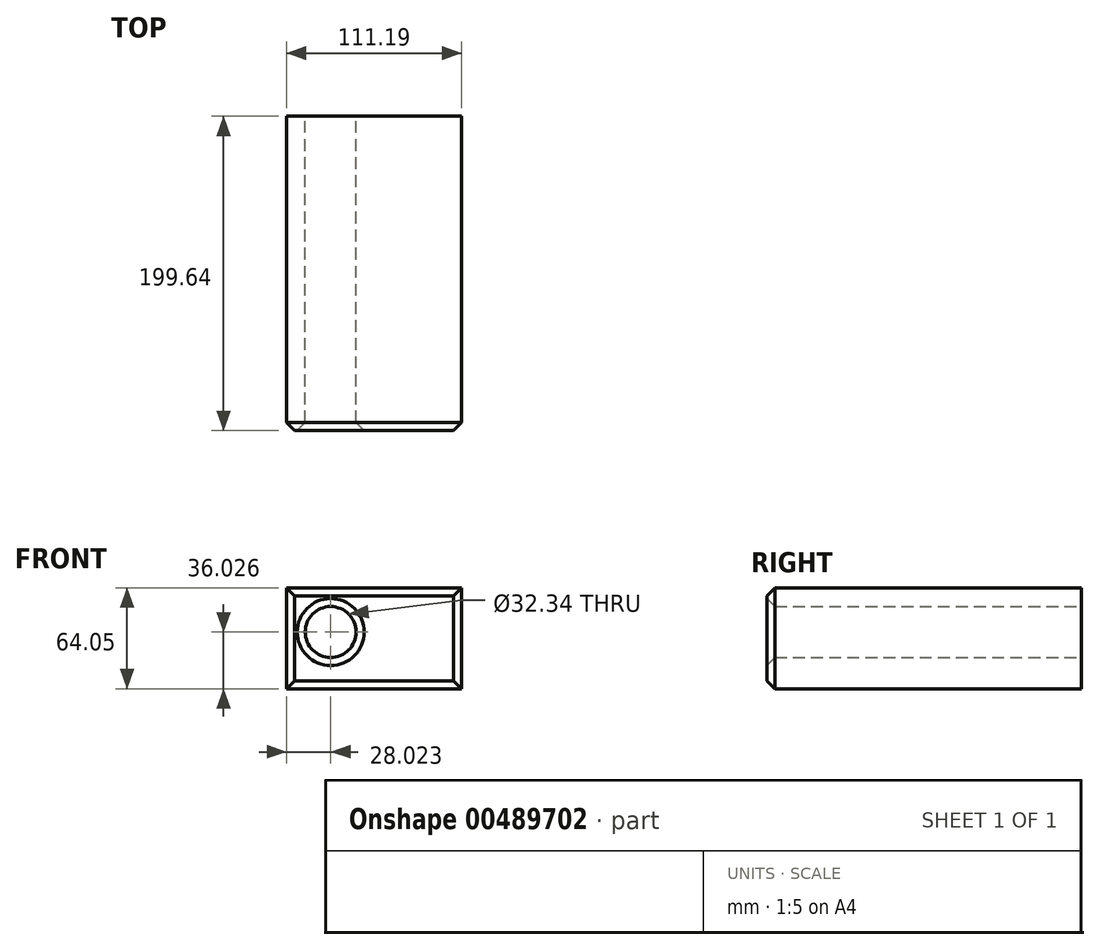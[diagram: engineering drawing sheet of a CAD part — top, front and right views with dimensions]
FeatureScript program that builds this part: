
annotation { "Feature Type Name" : "Feature", "Feature Type Description" : "" }
export const myFeature = defineFeature(function(context is Context, id is Id, definition is map)
    precondition{}
    {
        {
            var Q0;
            Q0=qCreatedBy(makeId("Front.planeOp"),FACE);
            var sketch = newSketch(context, id + "F0", { "sketchPlane" : qUnion([Q0])});
            skLineSegment(sketch, "E0.bottom", {"start": v(-129.12, -7.78) * mm, "end": v(-17.93, -7.78) * mm});
            skLineSegment(sketch, "E0.top", {"start": v(-129.12, -71.83) * mm, "end": v(-17.93, -71.83) * mm});
            skLineSegment(sketch, "E0.left", {"start": v(-129.12, -7.78) * mm, "end": v(-129.12, -71.83) * mm});
            skLineSegment(sketch, "E0.right", {"start": v(-17.93, -7.78) * mm, "end": v(-17.93, -71.83) * mm});
            skCircle(sketch, "E1", {"center": v(-101.1, -35.8) * mm, "radius": 16.17 * mm});
            skSolve(sketch);
        }
        {
            var Q0;
            Q0 = qSketchRegion(id + "F0", true);
            extrude(context, id + "F1", {"entities" : qUnion([Q0]), "depth" : 199.64 * mm});
        }
        {
            var Q0;
            Q0=makeQuery(id+"F1.opExtrude","CAP_FACE",FACE,{"disambiguationData":[OSD([sQuery(id+"F0.wireOp",EDGE,"E0.bottom"),sQuery(id+"F0.wireOp",EDGE,"E0.top"),sQuery(id+"F0.wireOp",EDGE,"E0.left"),sQuery(id+"F0.wireOp",EDGE,"E0.right"),sQuery(id+"F0.wireOp",EDGE,"E1")])],"isStart":false});
            chamfer(context, id + "F2", {"entities" : qUnion([Q0]), "width" : 5.08 * mm, "tangentPropagation" : true});
        }
        {
            var Q0;
            Q0=makeQuery(id+"F1.opExtrude","CAP_FACE",FACE,{"disambiguationData":[OSD([sQuery(id+"F0.wireOp",EDGE,"E0.bottom"),sQuery(id+"F0.wireOp",EDGE,"E0.top"),sQuery(id+"F0.wireOp",EDGE,"E0.left"),sQuery(id+"F0.wireOp",EDGE,"E0.right"),sQuery(id+"F0.wireOp",EDGE,"E1")])],"isStart":false});
            var sketch = newSketch(context, id + "F3", { "sketchPlane" : qUnion([Q0])});
            skLineSegment(sketch, "E2.bottom", {"start": v(-63.24, -25.15) * mm, "end": v(-40.18, -25.15) * mm});
            skLineSegment(sketch, "E2.top", {"start": v(-63.24, -55.7) * mm, "end": v(-40.18, -55.7) * mm});
            skLineSegment(sketch, "E2.left", {"start": v(-63.24, -25.15) * mm, "end": v(-63.24, -55.7) * mm});
            skLineSegment(sketch, "E2.right", {"start": v(-40.18, -25.15) * mm, "end": v(-40.18, -55.7) * mm});
            skArc(sketch, "E3", {"start": v(-63.24, -41) * mm, "mid": v(-60.74, -57.72) * mm, "end": v(-43.95, -55.7) * mm});
            skSolve(sketch);
        }
        {
            var Q0;
            {var subQ0=sQuery(id+"F3.wireOp",EDGE,"E2.left");var subQ1=sQuery(id+"F3.wireOp",EDGE,"E2.top");var subQ2=makeQuery(id+"F3.imprint","INTERSECT",VERTEX,{"derivedFrom":[subQ1,subQ0]});Q0=makeQuery(id+"F3.imprint","IMPRINT",FACE,{"disambiguationData":[TD([[makeQuery(id+"F3.imprint","IMPRINT",EDGE,{"disambiguationData":[TD([[subQ2,-1.0]])],"derivedFrom":subQ1}),1.0]])]});}
            var Q1;
            {var subQ0=sQuery(id+"F3.wireOp",EDGE,"E3");var subQ1=sQuery(id+"F3.wireOp",EDGE,"E2.top");var subQ2=makeQuery(id+"F3.imprint","INTERSECT",VERTEX,{"disambiguationData":[OD(0.0)],"derivedFrom":[subQ1,subQ0]});Q1=makeQuery(id+"F3.imprint","IMPRINT",FACE,{"disambiguationData":[TD([[makeQuery(id+"F3.imprint","IMPRINT",EDGE,{"disambiguationData":[TD([[subQ2,1.0]])],"derivedFrom":subQ1}),-1.0]])]});}
            var Q2;
            {var subQ0=sQuery(id+"F3.wireOp",EDGE,"E3");var subQ1=sQuery(id+"F3.wireOp",EDGE,"E2.left");var subQ2=makeQuery(id+"F3.imprint","INTERSECT",VERTEX,{"disambiguationData":[OD(0.0)],"derivedFrom":[subQ1,subQ0]});Q2=makeQuery(id+"F3.imprint","IMPRINT",FACE,{"disambiguationData":[TD([[makeQuery(id+"F3.imprint","IMPRINT",EDGE,{"disambiguationData":[TD([[subQ2,-1.0]])],"derivedFrom":subQ1}),-1.0]])]});}
            var Q3;
            {var subQ1=sQuery(id+"F3.wireOp",EDGE,"E2.bottom");Q3=makeQuery(id+"F3.imprint","IMPRINT",FACE,{"disambiguationData":[TD([[makeQuery(id+"F3.imprint","IMPRINT",EDGE,{"derivedFrom":subQ1}),-1.0]])]});}
            extrude(context, id + "F4", {"entities" : qUnion([Q0, Q1, Q2, Q3]), "operationType" : NewBodyOperationType.ADD, "oppositeDirection" : true, "depth" : 127 * mm});
        }
    });
